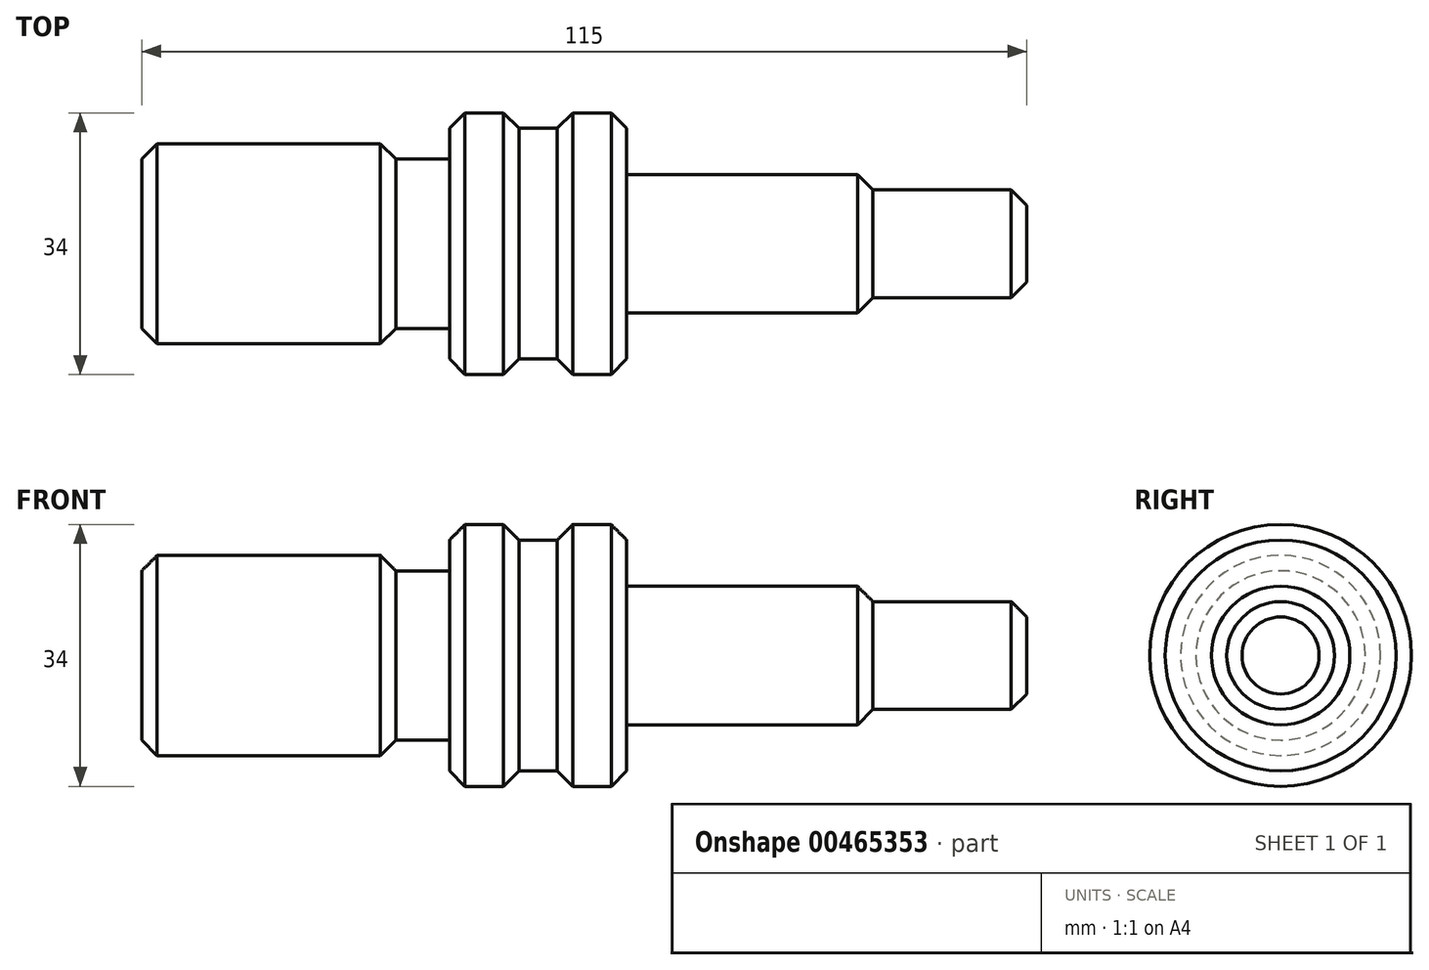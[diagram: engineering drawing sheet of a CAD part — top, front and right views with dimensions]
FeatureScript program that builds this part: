
annotation { "Feature Type Name" : "Feature", "Feature Type Description" : "" }
export const myFeature = defineFeature(function(context is Context, id is Id, definition is map)
    precondition{}
    {
        {
            var Q0;
            Q0=qCreatedBy(makeId("Front.planeOp"),FACE);
            var sketch = newSketch(context, id + "F0", { "sketchPlane" : qUnion([Q0])});
            skLineSegment(sketch, "E0.bottom", {"start": v(0, 0) * mm, "end": v(33, 0) * mm});
            skLineSegment(sketch, "E0.top", {"start": v(0, -13) * mm, "end": v(33, -13) * mm});
            skLineSegment(sketch, "E0.left", {"start": v(0, 0) * mm, "end": v(0, -13) * mm});
            skLineSegment(sketch, "E0.right", {"start": v(33, 0) * mm, "end": v(33, -13) * mm});
            skLineSegment(sketch, "E1.bottom", {"start": v(33, 0) * mm, "end": v(40, 0) * mm});
            skLineSegment(sketch, "E1.top", {"start": v(33, -11) * mm, "end": v(40, -11) * mm});
            skLineSegment(sketch, "E1.left", {"start": v(33, 0) * mm, "end": v(33, -11) * mm});
            skLineSegment(sketch, "E1.right", {"start": v(40, 0) * mm, "end": v(40, -11) * mm});
            skLineSegment(sketch, "E2.bottom", {"start": v(40, 0) * mm, "end": v(49, 0) * mm});
            skLineSegment(sketch, "E2.top", {"start": v(40, -17) * mm, "end": v(49, -17) * mm});
            skLineSegment(sketch, "E2.left", {"start": v(40, 0) * mm, "end": v(40, -17) * mm});
            skLineSegment(sketch, "E2.right", {"start": v(49, 0) * mm, "end": v(49, -17) * mm});
            skLineSegment(sketch, "E3.bottom", {"start": v(49, 0) * mm, "end": v(54, 0) * mm});
            skLineSegment(sketch, "E3.top", {"start": v(49, -15) * mm, "end": v(54, -15) * mm});
            skLineSegment(sketch, "E3.left", {"start": v(49, 0) * mm, "end": v(49, -15) * mm});
            skLineSegment(sketch, "E3.right", {"start": v(54, 0) * mm, "end": v(54, -15) * mm});
            skLineSegment(sketch, "E4.bottom", {"start": v(54, 0) * mm, "end": v(63, 0) * mm});
            skLineSegment(sketch, "E4.top", {"start": v(54, -17) * mm, "end": v(63, -17) * mm});
            skLineSegment(sketch, "E4.left", {"start": v(54, 0) * mm, "end": v(54, -17) * mm});
            skLineSegment(sketch, "E4.right", {"start": v(63, 0) * mm, "end": v(63, -17) * mm});
            skLineSegment(sketch, "E5.bottom", {"start": v(63, 0) * mm, "end": v(95, 0) * mm});
            skLineSegment(sketch, "E5.top", {"start": v(63, -9) * mm, "end": v(95, -9) * mm});
            skLineSegment(sketch, "E5.left", {"start": v(63, 0) * mm, "end": v(63, -9) * mm});
            skLineSegment(sketch, "E5.right", {"start": v(95, 0) * mm, "end": v(95, -9) * mm});
            skLineSegment(sketch, "E6.bottom", {"start": v(95, 0) * mm, "end": v(115, 0) * mm});
            skLineSegment(sketch, "E6.top", {"start": v(95, -7) * mm, "end": v(115, -7) * mm});
            skLineSegment(sketch, "E6.left", {"start": v(95, 0) * mm, "end": v(95, -7) * mm});
            skLineSegment(sketch, "E6.right", {"start": v(115, 0) * mm, "end": v(115, -7) * mm});
            skSolve(sketch);
        }
        {
            var Q0;
            Q0=makeQuery(id+"F0.imprint","IMPRINT",FACE,{"disambiguationData":[TD([[makeQuery(id+"F0.imprint","IMPRINT",EDGE,{"derivedFrom":sQuery(id+"F0.wireOp",EDGE,"E0.bottom")}),-1.0]])]});
            var Q1;
            {var subQ0=sQuery(id+"F0.wireOp",EDGE,"E1.bottom");Q1=makeQuery(id+"F0.imprint","IMPRINT",FACE,{"disambiguationData":[TD([[makeQuery(id+"F0.imprint","IMPRINT",EDGE,{"derivedFrom":subQ0}),-1.0]])]});}
            var Q2;
            {var subQ3=sQuery(id+"F0.wireOp",EDGE,"E2.bottom");Q2=makeQuery(id+"F0.imprint","IMPRINT",FACE,{"disambiguationData":[TD([[makeQuery(id+"F0.imprint","IMPRINT",EDGE,{"derivedFrom":subQ3}),-1.0]])]});}
            var Q3;
            {var subQ0=sQuery(id+"F0.wireOp",EDGE,"E3.bottom");Q3=makeQuery(id+"F0.imprint","IMPRINT",FACE,{"disambiguationData":[TD([[makeQuery(id+"F0.imprint","IMPRINT",EDGE,{"derivedFrom":subQ0}),-1.0]])]});}
            var Q4;
            {var subQ3=sQuery(id+"F0.wireOp",EDGE,"E4.bottom");Q4=makeQuery(id+"F0.imprint","IMPRINT",FACE,{"disambiguationData":[TD([[makeQuery(id+"F0.imprint","IMPRINT",EDGE,{"derivedFrom":subQ3}),-1.0]])]});}
            var Q5;
            Q5=makeQuery(id+"F0.imprint","IMPRINT",FACE,{"disambiguationData":[TD([[makeQuery(id+"F0.imprint","IMPRINT",EDGE,{"derivedFrom":sQuery(id+"F0.wireOp",EDGE,"E5.bottom")}),-1.0]])]});
            var Q6;
            Q6=makeQuery(id+"F0.imprint","IMPRINT",FACE,{"disambiguationData":[TD([[makeQuery(id+"F0.imprint","IMPRINT",EDGE,{"derivedFrom":sQuery(id+"F0.wireOp",EDGE,"E6.bottom")}),-1.0]])]});
            var Q7;
            Q7=sQuery(id+"F0.wireOp",EDGE,"E3.bottom");
            revolve(context, id + "F1", {"entities" : qUnion([Q0, Q1, Q2, Q3, Q4, Q5, Q6]), "axis" : qUnion([Q7]), "revolveType" : RevolveType.FULL});
        }
        {
            var Q0;
            Q0=makeQuery(id+"F1.opRevolve","SWEPT_FACE",FACE,{"disambiguationData":[OSD([sQuery(id+"F0.wireOp",EDGE,"E0.top")])]});
            var Q1;
            Q1=makeQuery(id+"F1.opRevolve","SWEPT_EDGE",EDGE,{"disambiguationData":[OSD([sQuery(id+"F0.wireOp",EDGE,"E2.top"),sQuery(id+"F0.wireOp",EDGE,"E2.left")])]});
            var Q2;
            Q2=makeQuery(id+"F1.opRevolve","SWEPT_EDGE",EDGE,{"disambiguationData":[OSD([sQuery(id+"F0.wireOp",EDGE,"E2.top"),sQuery(id+"F0.wireOp",EDGE,"E2.right")])]});
            var Q3;
            Q3=makeQuery(id+"F1.opRevolve","SWEPT_EDGE",EDGE,{"disambiguationData":[OSD([sQuery(id+"F0.wireOp",EDGE,"E4.top"),sQuery(id+"F0.wireOp",EDGE,"E4.left")])]});
            var Q4;
            Q4=makeQuery(id+"F1.opRevolve","SWEPT_EDGE",EDGE,{"disambiguationData":[OSD([sQuery(id+"F0.wireOp",EDGE,"E4.top"),sQuery(id+"F0.wireOp",EDGE,"E4.right")])]});
            var Q5;
            Q5=makeQuery(id+"F1.opRevolve","SWEPT_EDGE",EDGE,{"disambiguationData":[OSD([sQuery(id+"F0.wireOp",EDGE,"E5.top"),sQuery(id+"F0.wireOp",EDGE,"E5.right")])]});
            var Q6;
            Q6=makeQuery(id+"F1.opRevolve","SWEPT_EDGE",EDGE,{"disambiguationData":[OSD([sQuery(id+"F0.wireOp",EDGE,"E6.top"),sQuery(id+"F0.wireOp",EDGE,"E6.right")])]});
            chamfer(context, id + "F2", {"entities" : qUnion([Q0, Q1, Q2, Q3, Q4, Q5, Q6]), "width" : 2 * mm, "tangentPropagation" : true});
        }
    });
